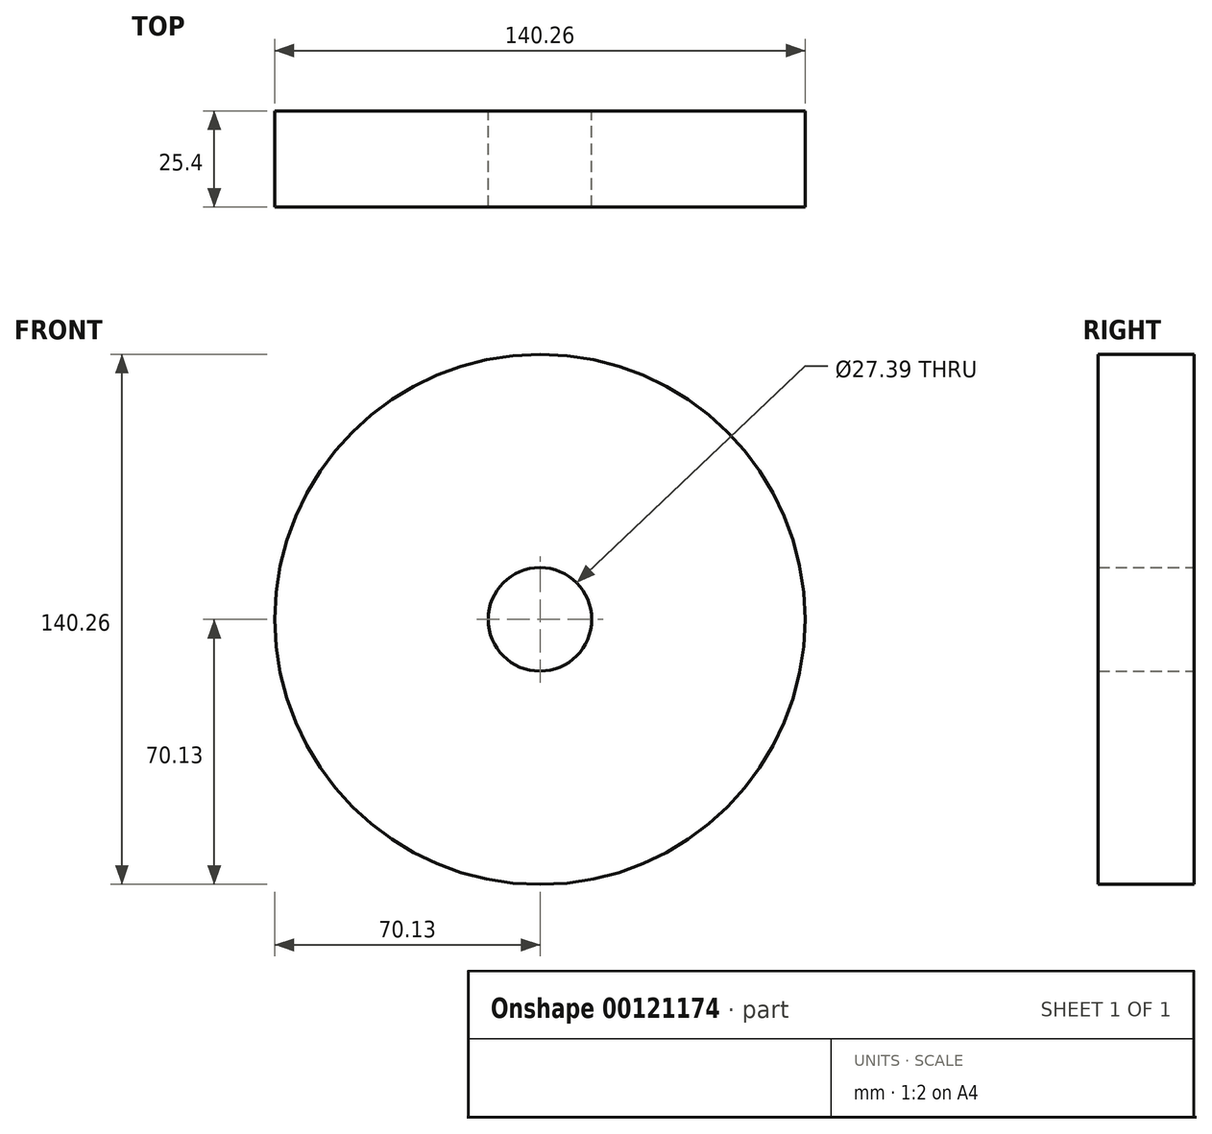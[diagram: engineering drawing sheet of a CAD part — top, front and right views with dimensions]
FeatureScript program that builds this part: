
annotation { "Feature Type Name" : "Feature", "Feature Type Description" : "" }
export const myFeature = defineFeature(function(context is Context, id is Id, definition is map)
    precondition{}
    {
        {
            var Q0;
            Q0=qCreatedBy(makeId("Front.planeOp"),FACE);
            var sketch = newSketch(context, id + "F0", { "sketchPlane" : qUnion([Q0])});
            skCircle(sketch, "E0", {"center": v(0, 0) * mm, "radius": 70.13 * mm});
            skCircle(sketch, "E1", {"center": v(0, 0) * mm, "radius": 13.7 * mm});
            skSolve(sketch);
        }
        {
            var Q0;
            Q0=qSketchRegion(id+"F0",true);
            extrude(context, id + "F1", {"entities" : qUnion([Q0]), "endBound" : BoundingType.SYMMETRIC, "depth" : 25.4 * mm});
        }
    });
